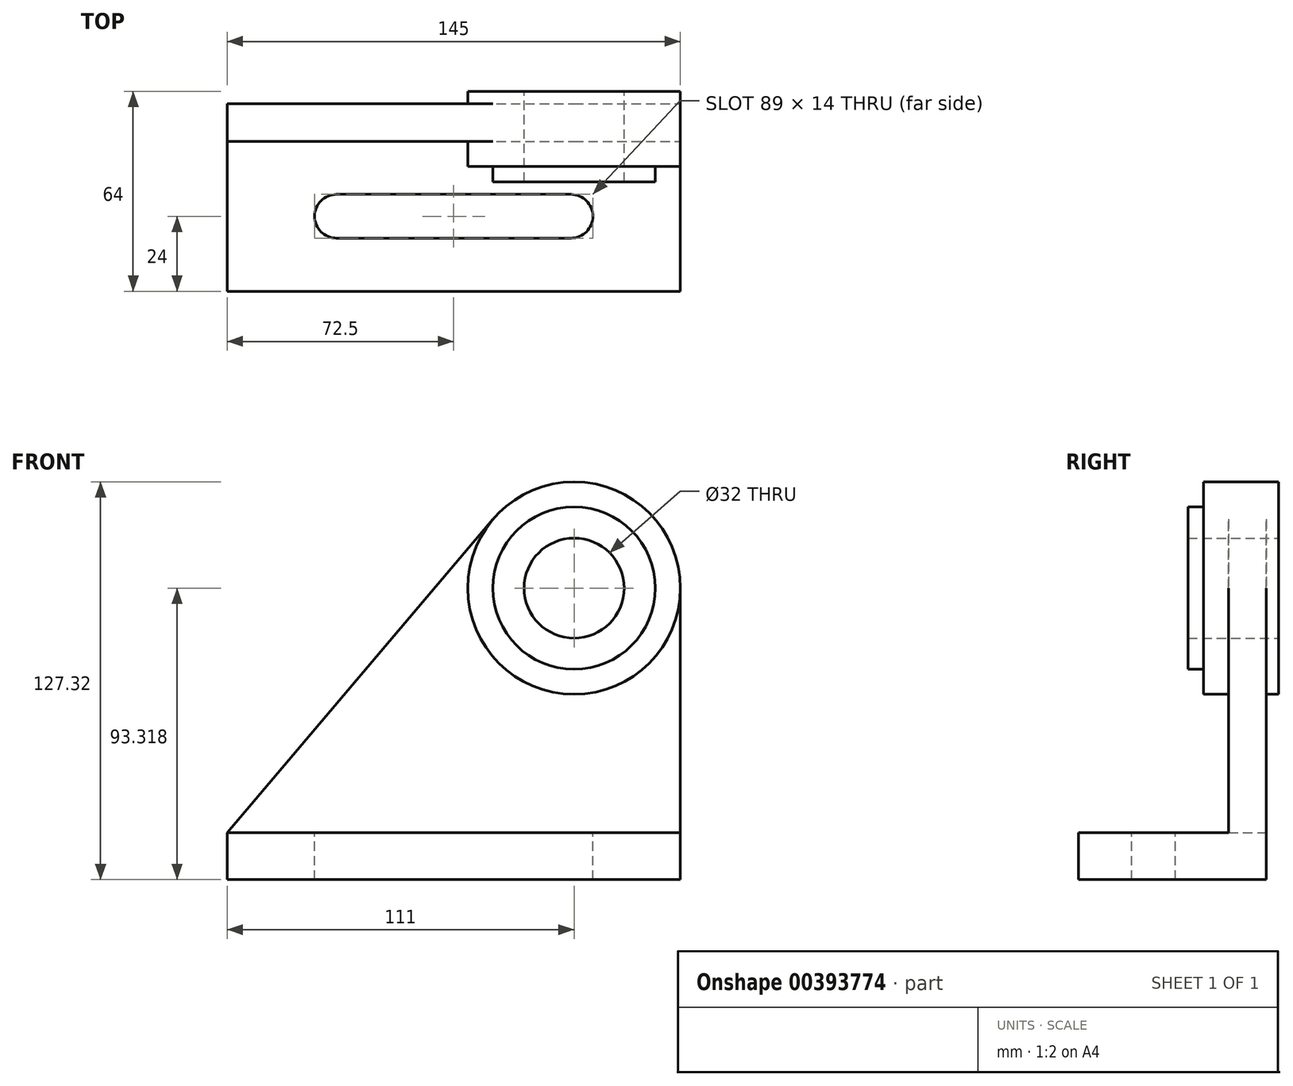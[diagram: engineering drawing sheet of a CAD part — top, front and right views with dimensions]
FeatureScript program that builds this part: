
annotation { "Feature Type Name" : "Feature", "Feature Type Description" : "" }
export const myFeature = defineFeature(function(context is Context, id is Id, definition is map)
    precondition{}
    {
        {
            var Q0;
            Q0=qCreatedBy(makeId("Front.planeOp"),FACE);
            var sketch = newSketch(context, id + "F0", { "sketchPlane" : qUnion([Q0])});
            skLineSegment(sketch, "E0.bottom", {"start": v(-72.5, -12.71) * mm, "end": v(72.5, -12.71) * mm});
            skLineSegment(sketch, "E0.top", {"start": v(-72.5, -27.71) * mm, "end": v(72.5, -27.71) * mm});
            skLineSegment(sketch, "E0.left", {"start": v(-72.5, -12.71) * mm, "end": v(-72.5, -27.71) * mm});
            skLineSegment(sketch, "E0.right", {"start": v(72.5, -12.71) * mm, "end": v(72.5, -27.71) * mm});
            skCircle(sketch, "E1", {"center": v(38.5, 65.6) * mm, "radius": 34 * mm});
            skCircle(sketch, "E2", {"center": v(38.5, 65.6) * mm, "radius": 26 * mm});
            skCircle(sketch, "E3", {"center": v(38.5, 65.6) * mm, "radius": 16 * mm});
            skLineSegment(sketch, "E4", {"start": v(72.5, -12.71) * mm, "end": v(72.5, 65.6) * mm});
            skLineSegment(sketch, "E5", {"start": v(-72.5, -12.71) * mm, "end": v(12.57, 87.6) * mm});
            skSolve(sketch);
        }
        {
            var Q0;
            Q0=makeQuery(id+"F0.imprint","IMPRINT",FACE,{"disambiguationData":[TD([[makeQuery(id+"F0.imprint","IMPRINT",EDGE,{"derivedFrom":sQuery(id+"F0.wireOp",EDGE,"E0.bottom")}),-1.0]])]});
            extrude(context, id + "F1", {"entities" : qUnion([Q0]), "depth" : 60 * mm});
        }
        {
            var Q0;
            Q0=makeQuery(id+"F0.imprint","IMPRINT",FACE,{"disambiguationData":[TD([[makeQuery(id+"F0.imprint","IMPRINT",EDGE,{"derivedFrom":sQuery(id+"F0.wireOp",EDGE,"E0.bottom")}),1.0]])]});
            extrude(context, id + "F2", {"entities" : qUnion([Q0]), "operationType" : NewBodyOperationType.ADD, "depth" : 12 * mm});
        }
        {
            var Q0;
            Q0=makeQuery(id+"F0.imprint","IMPRINT",FACE,{"disambiguationData":[TD([[makeQuery(id+"F0.imprint","IMPRINT",EDGE,{"derivedFrom":sQuery(id+"F0.wireOp",EDGE,"E2")}),-1.0]])]});
            extrude(context, id + "F3", {"entities" : qUnion([Q0]), "operationType" : NewBodyOperationType.ADD, "depth" : 20 * mm});
        }
        {
            var Q0;
            Q0=makeQuery(id+"F0.imprint","IMPRINT",FACE,{"disambiguationData":[TD([[makeQuery(id+"F0.imprint","IMPRINT",EDGE,{"derivedFrom":sQuery(id+"F0.wireOp",EDGE,"E2")}),1.0]])]});
            extrude(context, id + "F4", {"entities" : qUnion([Q0]), "operationType" : NewBodyOperationType.ADD, "depth" : 25 * mm});
        }
        {
            var Q0;
            Q0=makeQuery(id+"F1.opExtrude","SWEPT_FACE",FACE,{"disambiguationData":[OSD([sQuery(id+"F0.wireOp",EDGE,"E0.bottom")])]});
            var sketch = newSketch(context, id + "F5", { "sketchPlane" : qUnion([Q0])});
            skArc(sketch, "E6", {"start": v(-37.5, -29) * mm, "mid": v(-44.5, -36) * mm, "end": v(-37.5, -43) * mm});
            skArc(sketch, "E7", {"start": v(37.5, -43) * mm, "mid": v(44.5, -36) * mm, "end": v(37.5, -29) * mm});
            skLineSegment(sketch, "E8", {"start": v(-37.5, -43) * mm, "end": v(37.5, -43) * mm});
            skLineSegment(sketch, "E9", {"start": v(-37.5, -29) * mm, "end": v(37.5, -29) * mm});
            skSolve(sketch);
        }
        {
            var Q0;
            Q0=makeQuery(id+"F5.imprint","IMPRINT",FACE,{"disambiguationData":[TD([[makeQuery(id+"F5.imprint","IMPRINT",EDGE,{"derivedFrom":sQuery(id+"F5.wireOp",EDGE,"E6")}),1.0]])]});
            extrude(context, id + "F6", {"entities" : qUnion([Q0]), "operationType" : NewBodyOperationType.REMOVE, "oppositeDirection" : true, "depth" : 25 * mm});
        }
        {
            var Q0;
            Q0=makeQuery(id+"F0.imprint","IMPRINT",FACE,{"disambiguationData":[TD([[makeQuery(id+"F0.imprint","IMPRINT",EDGE,{"derivedFrom":sQuery(id+"F0.wireOp",EDGE,"E2")}),-1.0]])]});
            var Q1;
            Q1=makeQuery(id+"F0.imprint","IMPRINT",FACE,{"disambiguationData":[TD([[makeQuery(id+"F0.imprint","IMPRINT",EDGE,{"derivedFrom":sQuery(id+"F0.wireOp",EDGE,"E2")}),1.0]])]});
            extrude(context, id + "F7", {"entities" : qUnion([Q0, Q1]), "operationType" : NewBodyOperationType.ADD, "oppositeDirection" : true, "depth" : 4 * mm});
        }
    });
